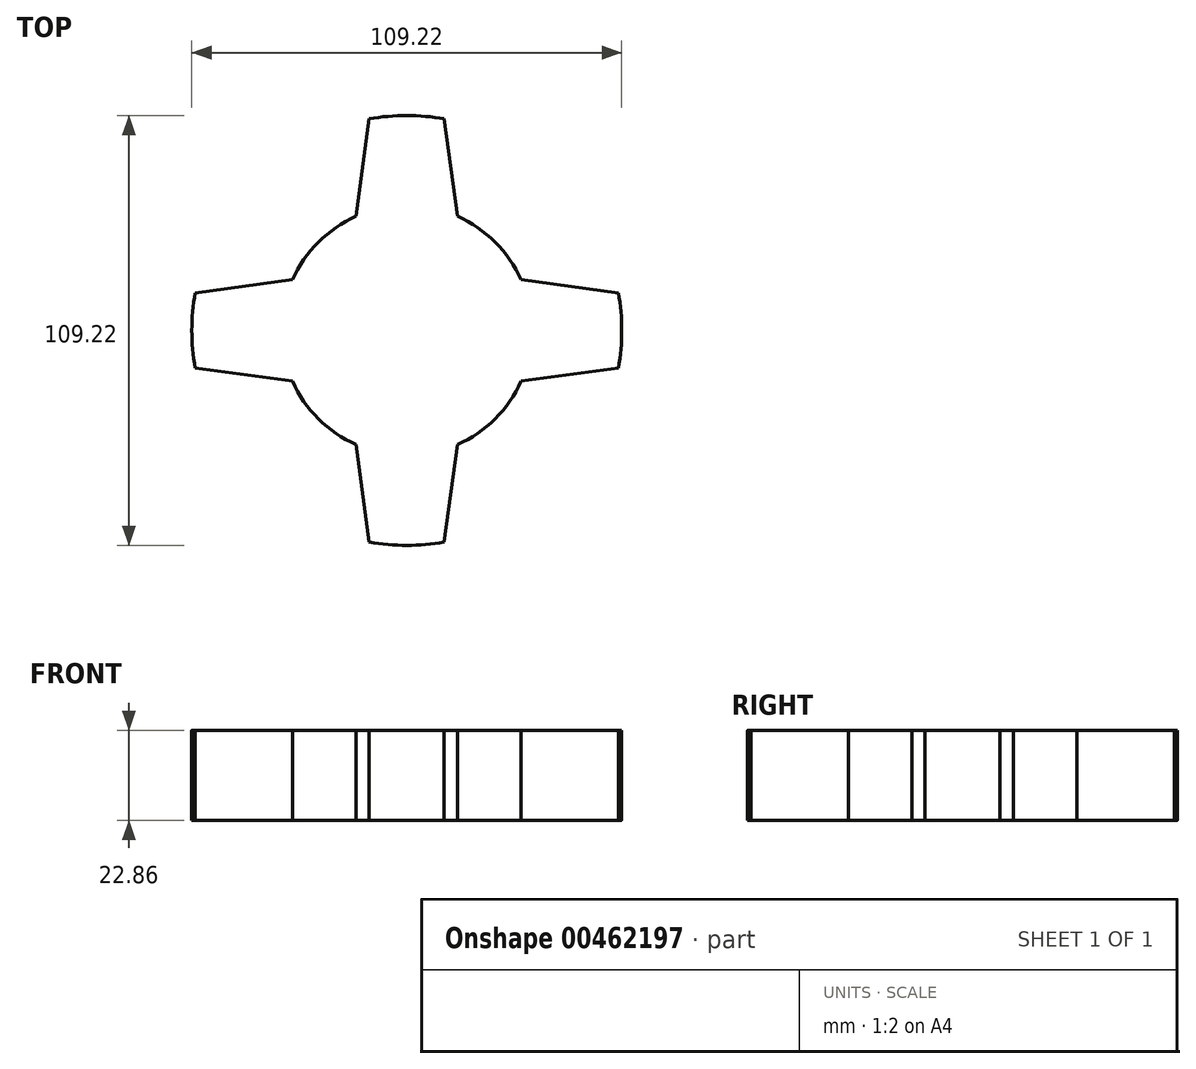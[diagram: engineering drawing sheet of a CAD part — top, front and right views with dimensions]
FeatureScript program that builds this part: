
annotation { "Feature Type Name" : "Feature", "Feature Type Description" : "" }
export const myFeature = defineFeature(function(context is Context, id is Id, definition is map)
    precondition{}
    {
        {
            var Q0;
            Q0=qCreatedBy(makeId("Top.planeOp"),FACE);
            var sketch = newSketch(context, id + "F0", { "sketchPlane" : qUnion([Q0])});
            skCircle(sketch, "E0", {"center": v(0, 0) * mm, "radius": 31.75 * mm});
            skArc(sketch, "E1", {"start": v(-53.77, 9.52) * mm, "mid": v(-54.61, 0) * mm, "end": v(-53.77, -9.53) * mm});
            skLineSegment(sketch, "E2", {"start": v(-26.67, 0) * mm, "end": v(-26.67, 13.2) * mm});
            skLineSegment(sketch, "E3", {"start": v(-26.67, 13.2) * mm, "end": v(-53.77, 9.52) * mm});
            skLineSegment(sketch, "E4.MirrorCS", {"start": v(-26.67, 0) * mm, "end": v(-26.67, -13.2) * mm});
            skLineSegment(sketch, "E5.MirrorCS", {"start": v(-26.67, -13.2) * mm, "end": v(-53.77, -9.52) * mm});
            skLineSegment(sketch, "E6.1.0", {"start": v(0, -26.67) * mm, "end": v(-13.2, -26.67) * mm});
            skLineSegment(sketch, "E6.1.1", {"start": v(-13.2, -26.67) * mm, "end": v(-9.53, -53.77) * mm});
            skLineSegment(sketch, "E6.1.2", {"start": v(13.2, -26.67) * mm, "end": v(9.52, -53.77) * mm});
            skLineSegment(sketch, "E6.1.3", {"start": v(0, -26.67) * mm, "end": v(13.2, -26.67) * mm});
            skArc(sketch, "E6.1.4", {"start": v(-9.52, -53.77) * mm, "mid": v(0, -54.61) * mm, "end": v(9.53, -53.77) * mm});
            skLineSegment(sketch, "E6.2.0", {"start": v(26.67, 0) * mm, "end": v(26.67, -13.2) * mm});
            skLineSegment(sketch, "E6.2.1", {"start": v(26.67, -13.2) * mm, "end": v(53.77, -9.53) * mm});
            skLineSegment(sketch, "E6.2.2", {"start": v(26.67, 13.2) * mm, "end": v(53.77, 9.52) * mm});
            skLineSegment(sketch, "E6.2.3", {"start": v(26.67, 0) * mm, "end": v(26.67, 13.2) * mm});
            skArc(sketch, "E6.2.4", {"start": v(53.77, -9.52) * mm, "mid": v(54.61, 0) * mm, "end": v(53.77, 9.53) * mm});
            skLineSegment(sketch, "E6.3.0", {"start": v(0, 26.67) * mm, "end": v(13.2, 26.67) * mm});
            skLineSegment(sketch, "E6.3.1", {"start": v(13.2, 26.67) * mm, "end": v(9.53, 53.77) * mm});
            skLineSegment(sketch, "E6.3.2", {"start": v(-13.2, 26.67) * mm, "end": v(-9.52, 53.77) * mm});
            skLineSegment(sketch, "E6.3.3", {"start": v(0, 26.67) * mm, "end": v(-13.2, 26.67) * mm});
            skArc(sketch, "E6.3.4", {"start": v(9.52, 53.77) * mm, "mid": v(0, 54.61) * mm, "end": v(-9.53, 53.77) * mm});
            skSolve(sketch);
        }
        {
            var Q0;
            Q0=makeQuery(id+"F0.imprint","IMPRINT",FACE,{"disambiguationData":[TD([[makeQuery(id+"F0.imprint","IMPRINT",EDGE,{"derivedFrom":sQuery(id+"F0.wireOp",EDGE,"E0")}),1.0]])]});
            var Q1;
            {var subQ2=sQuery(id+"F0.wireOp",EDGE,"E2");Q1=makeQuery(id+"F0.imprint","IMPRINT",FACE,{"disambiguationData":[TD([[makeQuery(id+"F0.imprint","IMPRINT",EDGE,{"derivedFrom":subQ2}),1.0]])]});}
            var Q2;
            {var subQ5=sQuery(id+"F0.wireOp",EDGE,"E1");Q2=makeQuery(id+"F0.imprint","IMPRINT",FACE,{"disambiguationData":[TD([[makeQuery(id+"F0.imprint","IMPRINT",EDGE,{"derivedFrom":subQ5}),1.0]])]});}
            var Q3;
            {var subQ5=sQuery(id+"F0.wireOp",EDGE,"E6.1.4");Q3=makeQuery(id+"F0.imprint","IMPRINT",FACE,{"disambiguationData":[TD([[makeQuery(id+"F0.imprint","IMPRINT",EDGE,{"derivedFrom":subQ5}),1.0]])]});}
            var Q4;
            {var subQ5=sQuery(id+"F0.wireOp",EDGE,"E6.1.0");Q4=makeQuery(id+"F0.imprint","IMPRINT",FACE,{"disambiguationData":[TD([[makeQuery(id+"F0.imprint","IMPRINT",EDGE,{"derivedFrom":subQ5}),1.0]])]});}
            var Q5;
            {var subQ5=sQuery(id+"F0.wireOp",EDGE,"E6.2.0");Q5=makeQuery(id+"F0.imprint","IMPRINT",FACE,{"disambiguationData":[TD([[makeQuery(id+"F0.imprint","IMPRINT",EDGE,{"derivedFrom":subQ5}),1.0]])]});}
            var Q6;
            {var subQ5=sQuery(id+"F0.wireOp",EDGE,"E6.2.4");Q6=makeQuery(id+"F0.imprint","IMPRINT",FACE,{"disambiguationData":[TD([[makeQuery(id+"F0.imprint","IMPRINT",EDGE,{"derivedFrom":subQ5}),1.0]])]});}
            var Q7;
            {var subQ5=sQuery(id+"F0.wireOp",EDGE,"E6.3.0");Q7=makeQuery(id+"F0.imprint","IMPRINT",FACE,{"disambiguationData":[TD([[makeQuery(id+"F0.imprint","IMPRINT",EDGE,{"derivedFrom":subQ5}),1.0]])]});}
            var Q8;
            {var subQ5=sQuery(id+"F0.wireOp",EDGE,"E6.3.4");Q8=makeQuery(id+"F0.imprint","IMPRINT",FACE,{"disambiguationData":[TD([[makeQuery(id+"F0.imprint","IMPRINT",EDGE,{"derivedFrom":subQ5}),1.0]])]});}
            extrude(context, id + "F1", {"entities" : qUnion([Q0, Q1, Q2, Q3, Q4, Q5, Q6, Q7, Q8]), "depth" : 22.86 * mm});
        }
    });
